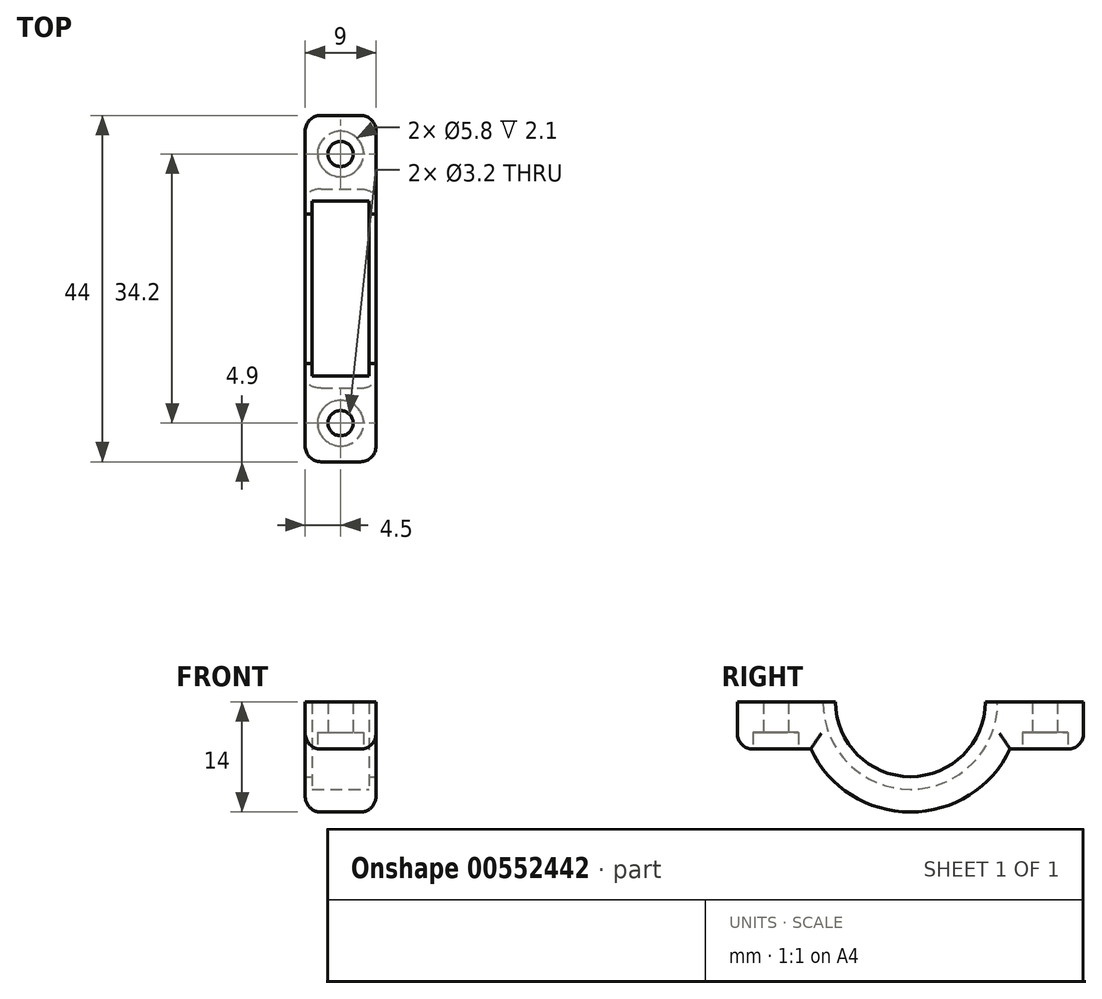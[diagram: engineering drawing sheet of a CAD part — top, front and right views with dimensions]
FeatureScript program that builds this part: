
annotation { "Feature Type Name" : "Feature", "Feature Type Description" : "" }
export const myFeature = defineFeature(function(context is Context, id is Id, definition is map)
    precondition{}
    {
        {
            var Q0;
            Q0=qCreatedBy(makeId("Top.planeOp"),FACE);
            var sketch = newSketch(context, id + "F0", { "sketchPlane" : qUnion([Q0])});
            skLineSegment(sketch, "E0", {"start": v(0, 11.1) * mm, "end": v(3.6, 11.1) * mm});
            skLineSegment(sketch, "E1", {"start": v(3.6, 11.1) * mm, "end": v(3.6, 9.5) * mm});
            skLineSegment(sketch, "E2", {"start": v(3.6, 9.5) * mm, "end": v(4.5, 9.5) * mm});
            skLineSegment(sketch, "E3", {"start": v(4.5, 9.5) * mm, "end": v(4.5, 14) * mm});
            skLineSegment(sketch, "E4", {"start": v(4.5, 14) * mm, "end": v(0, 14) * mm});
            skLineSegment(sketch, "E5", {"start": v(0, 16.16) * mm, "end": v(0, -15.66) * mm, "construction": true});
            skLineSegment(sketch, "E6", {"start": v(15.48, 0) * mm, "end": v(-13.35, 0) * mm, "construction": true});
            skLineSegment(sketch, "E7.MirrorCS", {"start": v(0, 11.1) * mm, "end": v(-3.6, 11.1) * mm});
            skLineSegment(sketch, "E8.MirrorCS", {"start": v(-3.6, 11.1) * mm, "end": v(-3.6, 9.5) * mm});
            skLineSegment(sketch, "E9.MirrorCS", {"start": v(-3.6, 9.5) * mm, "end": v(-4.5, 9.5) * mm});
            skLineSegment(sketch, "E10.MirrorCS", {"start": v(-4.5, 9.5) * mm, "end": v(-4.5, 14) * mm});
            skLineSegment(sketch, "E11.MirrorCS", {"start": v(-4.5, 14) * mm, "end": v(0, 14) * mm});
            skSolve(sketch);
        }
        {
            var Q0;
            Q0 = qSketchRegion(id + "F0", true);
            var Q1;
            Q1=sQuery(id+"F0.wireOp",EDGE,"E7.MirrorCS");
            var Q2;
            Q2=sQuery(id+"F0.wireOp",EDGE,"E0");
            var Q3;
            Q3=sQuery(id+"F0.wireOp",EDGE,"E1");
            var Q4;
            Q4=sQuery(id+"F0.wireOp",EDGE,"E2");
            var Q5;
            Q5=sQuery(id+"F0.wireOp",EDGE,"E3");
            var Q6;
            Q6=sQuery(id+"F0.wireOp",EDGE,"E4");
            var Q7;
            Q7=sQuery(id+"F0.wireOp",EDGE,"E11.MirrorCS");
            var Q8;
            Q8=sQuery(id+"F0.wireOp",EDGE,"E10.MirrorCS");
            var Q9;
            Q9=sQuery(id+"F0.wireOp",EDGE,"E9.MirrorCS");
            var Q10;
            Q10=sQuery(id+"F0.wireOp",EDGE,"E8.MirrorCS");
            var Q11;
            Q11=sQuery(id+"F0.wireOp",EDGE,"E6");
            revolve(context, id + "F1", {"entities" : qUnion([Q0]), "surfaceEntities" : qUnion([Q1, Q2, Q3, Q4, Q5, Q6, Q7, Q8, Q9, Q10]), "axis" : qUnion([Q11]), "revolveType" : RevolveType.ONE_DIRECTION, "angle" : 180 * degree});
        }
        {
            var Q0;
            Q0=qCreatedBy(makeId("Top.planeOp"),FACE);
            var sketch = newSketch(context, id + "F2", { "sketchPlane" : qUnion([Q0])});
            skLineSegment(sketch, "E12", {"start": v(-4.5, 11.1) * mm, "end": v(4.5, 11.1) * mm});
            skLineSegment(sketch, "E13", {"start": v(4.5, 11.1) * mm, "end": v(4.5, 22) * mm});
            skLineSegment(sketch, "E14", {"start": v(4.5, 22) * mm, "end": v(-4.5, 22) * mm});
            skLineSegment(sketch, "E15", {"start": v(-4.5, 22) * mm, "end": v(-4.5, 11.1) * mm});
            skLineSegment(sketch, "E16", {"start": v(-19.32, 0) * mm, "end": v(20.85, 0) * mm, "construction": true});
            skLineSegment(sketch, "E17.MirrorCS", {"start": v(-4.5, -22) * mm, "end": v(-4.5, -11.1) * mm});
            skLineSegment(sketch, "E18.MirrorCS", {"start": v(-4.5, -11.1) * mm, "end": v(4.5, -11.1) * mm});
            skLineSegment(sketch, "E19.MirrorCS", {"start": v(4.5, -11.1) * mm, "end": v(4.5, -22) * mm});
            skLineSegment(sketch, "E20.MirrorCS", {"start": v(4.5, -22) * mm, "end": v(-4.5, -22) * mm});
            skSolve(sketch);
        }
        {
            var Q0;
            Q0 = qSketchRegion(id + "F2", true);
            extrude(context, id + "F3", {"entities" : qUnion([Q0]), "operationType" : NewBodyOperationType.ADD, "oppositeDirection" : true, "depth" : 6 * mm, "offsetDistance" : 25 * mm});
        }
        {
            var Q0;
            Q0=makeQuery(id+"F3.opExtrude","SWEPT_EDGE",EDGE,{"disambiguationData":[OSD([sQuery(id+"F2.wireOp",EDGE,"E17.MirrorCS"),sQuery(id+"F2.wireOp",EDGE,"E20.MirrorCS")])]});
            var Q1;
            Q1=makeQuery(id+"F3.opExtrude","SWEPT_EDGE",EDGE,{"disambiguationData":[OSD([sQuery(id+"F2.wireOp",EDGE,"E19.MirrorCS"),sQuery(id+"F2.wireOp",EDGE,"E20.MirrorCS")])]});
            var Q2;
            Q2=makeQuery(id+"F1.opRevolve","SWEPT_EDGE",EDGE,{"disambiguationData":[OSD([sQuery(id+"F0.wireOp",EDGE,"E10.MirrorCS"),sQuery(id+"F0.wireOp",EDGE,"E11.MirrorCS")])]});
            var Q3;
            Q3=makeQuery(id+"F3.opExtrude","CAP_EDGE",EDGE,{"disambiguationData":[OSD([sQuery(id+"F2.wireOp",EDGE,"E17.MirrorCS")])],"isStart":false});
            var Q4;
            Q4=makeQuery(id+"F3.opExtrude","CAP_EDGE",EDGE,{"disambiguationData":[OSD([sQuery(id+"F2.wireOp",EDGE,"E19.MirrorCS")])],"isStart":false});
            var Q5;
            Q5=makeQuery(id+"F3.opExtrude","CAP_EDGE",EDGE,{"disambiguationData":[OSD([sQuery(id+"F2.wireOp",EDGE,"E20.MirrorCS")])],"isStart":false});
            var Q6;
            Q6=makeQuery(id+"F1.opRevolve","SWEPT_EDGE",EDGE,{"disambiguationData":[OSD([sQuery(id+"F0.wireOp",EDGE,"E3"),sQuery(id+"F0.wireOp",EDGE,"E4")])]});
            var Q7;
            Q7=makeQuery(id+"F3.opExtrude","CAP_EDGE",EDGE,{"disambiguationData":[OSD([sQuery(id+"F2.wireOp",EDGE,"E15")])],"isStart":false});
            var Q8;
            Q8=makeQuery(id+"F3.opExtrude","SWEPT_EDGE",EDGE,{"disambiguationData":[OSD([sQuery(id+"F2.wireOp",EDGE,"E14"),sQuery(id+"F2.wireOp",EDGE,"E15")])]});
            var Q9;
            Q9=makeQuery(id+"F3.opExtrude","SWEPT_EDGE",EDGE,{"disambiguationData":[OSD([sQuery(id+"F2.wireOp",EDGE,"E13"),sQuery(id+"F2.wireOp",EDGE,"E14")])]});
            var Q10;
            Q10=makeQuery(id+"F3.opExtrude","CAP_EDGE",EDGE,{"disambiguationData":[OSD([sQuery(id+"F2.wireOp",EDGE,"E14")])],"isStart":false});
            var Q11;
            Q11=makeQuery(id+"F3.opExtrude","CAP_EDGE",EDGE,{"disambiguationData":[OSD([sQuery(id+"F2.wireOp",EDGE,"E13")])],"isStart":false});
            fillet(context, id + "F4", {"entities" : qUnion([Q0, Q1, Q2, Q3, Q4, Q5, Q6, Q7, Q8, Q9, Q10, Q11]), "radius" : 2 * mm, "tangentPropagation" : true, "allowEdgeOverflow" : false});
        }
        {
            var Q0;
            Q0=makeQuery(id+"F3.opExtrude","CAP_FACE",FACE,{"disambiguationData":[OSD([sQuery(id+"F2.wireOp",EDGE,"E12"),sQuery(id+"F2.wireOp",EDGE,"E13"),sQuery(id+"F2.wireOp",EDGE,"E14"),sQuery(id+"F2.wireOp",EDGE,"E15")])],"isStart":false});
            var sketch = newSketch(context, id + "F5", { "sketchPlane" : qUnion([Q0])});
            skCircle(sketch, "E21", {"center": v(0, -17.1) * mm, "radius": 2.9 * mm});
            skCircle(sketch, "E22.MirrorC", {"center": v(0, 17.1) * mm, "radius": 2.9 * mm});
            skSolve(sketch);
        }
        {
            var Q0;
            Q0 = qSketchRegion(id + "F5", true);
            extrude(context, id + "F6", {"entities" : qUnion([Q0]), "operationType" : NewBodyOperationType.REMOVE, "oppositeDirection" : true, "depth" : 2.1 * mm, "offsetDistance" : 25 * mm});
        }
        {
            var Q0;
            Q0=makeQuery(id+"F6.boolean.opBoolean","COPY",FACE,{"derivedFrom":makeQuery(id+"F6.opExtrude","CAP_FACE",FACE,{"disambiguationData":[OSD([sQuery(id+"F5.wireOp",EDGE,"E21")])],"isStart":false})});
            var sketch = newSketch(context, id + "F7", { "sketchPlane" : qUnion([Q0])});
            skCircle(sketch, "E23", {"center": v(0, -17.1) * mm, "radius": 1.6 * mm});
            skCircle(sketch, "E24.MirrorC", {"center": v(0, 17.1) * mm, "radius": 1.6 * mm});
            skSolve(sketch);
        }
        {
            var Q0;
            Q0 = qSketchRegion(id + "F7", true);
            extrude(context, id + "F8", {"entities" : qUnion([Q0]), "operationType" : NewBodyOperationType.REMOVE, "endBound" : BoundingType.THROUGH_ALL, "oppositeDirection" : true, "depth" : 25 * mm, "offsetDistance" : 25 * mm});
        }
    });
